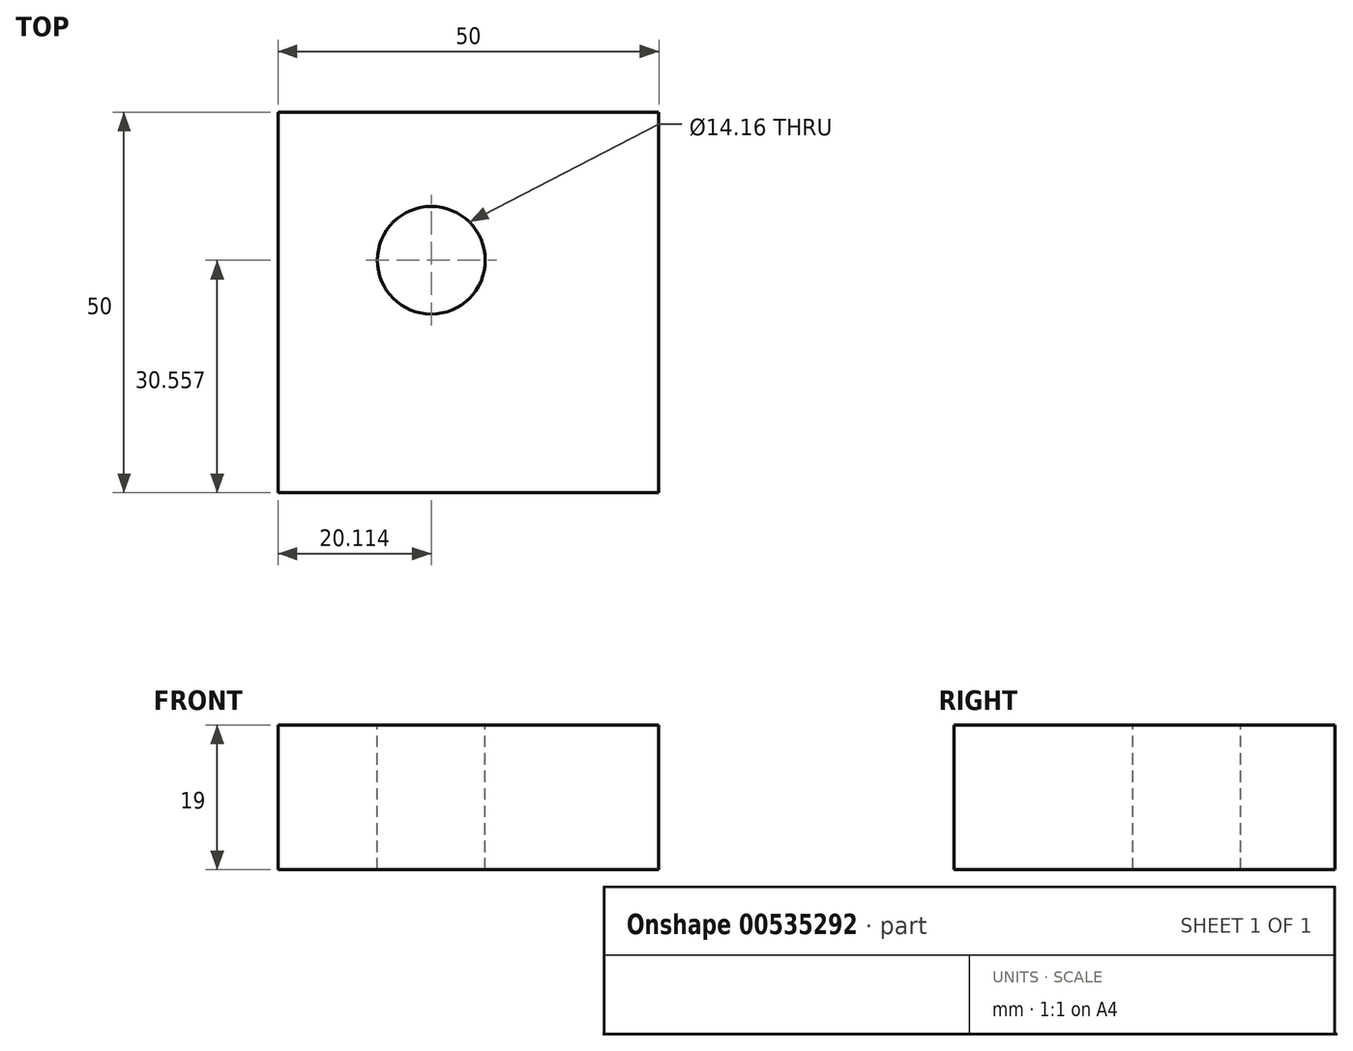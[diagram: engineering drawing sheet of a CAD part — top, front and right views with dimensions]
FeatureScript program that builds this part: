
annotation { "Feature Type Name" : "Feature", "Feature Type Description" : "" }
export const myFeature = defineFeature(function(context is Context, id is Id, definition is map)
    precondition{}
    {
        {
            var Q0;
            Q0=qCreatedBy(makeId("Top.planeOp"),FACE);
            var sketch = newSketch(context, id + "F0", { "sketchPlane" : qUnion([Q0])});
            skLineSegment(sketch, "E0.bottom", {"start": v(-70.16, 22.05) * mm, "end": v(-20.16, 22.05) * mm});
            skLineSegment(sketch, "E0.top", {"start": v(-70.16, -27.95) * mm, "end": v(-20.16, -27.95) * mm});
            skLineSegment(sketch, "E0.left", {"start": v(-70.16, 22.05) * mm, "end": v(-70.16, -27.95) * mm});
            skLineSegment(sketch, "E0.right", {"start": v(-20.16, 22.05) * mm, "end": v(-20.16, -27.95) * mm});
            skSolve(sketch);
        }
        {
            var Q0;
            Q0=makeQuery(id+"F0.imprint","IMPRINT",FACE,{"disambiguationData":[TD([[makeQuery(id+"F0.imprint","IMPRINT",EDGE,{"derivedFrom":sQuery(id+"F0.wireOp",EDGE,"E0.bottom")}),-1.0]])]});
            extrude(context, id + "F1", {"entities" : qUnion([Q0]), "depth" : 19 * mm, "offsetDistance" : 25 * mm});
        }
        {
            var Q0;
            Q0=makeQuery(id+"F1.opExtrude","CAP_FACE",FACE,{"disambiguationData":[OSD([sQuery(id+"F0.wireOp",EDGE,"E0.bottom"),sQuery(id+"F0.wireOp",EDGE,"E0.top"),sQuery(id+"F0.wireOp",EDGE,"E0.left"),sQuery(id+"F0.wireOp",EDGE,"E0.right")])],"isStart":false});
            var sketch = newSketch(context, id + "F2", { "sketchPlane" : qUnion([Q0])});
            skCircle(sketch, "E1", {"center": v(-50.05, 2.6) * mm, "radius": 7.08 * mm});
            skSolve(sketch);
        }
        {
            var Q0;
            Q0 = qSketchRegion(id + "F2", true);
            extrude(context, id + "F3", {"entities" : qUnion([Q0]), "operationType" : NewBodyOperationType.REMOVE, "endBound" : BoundingType.UP_TO_NEXT, "oppositeDirection" : true, "depth" : 25 * mm, "offsetDistance" : 25 * mm});
        }
    });
